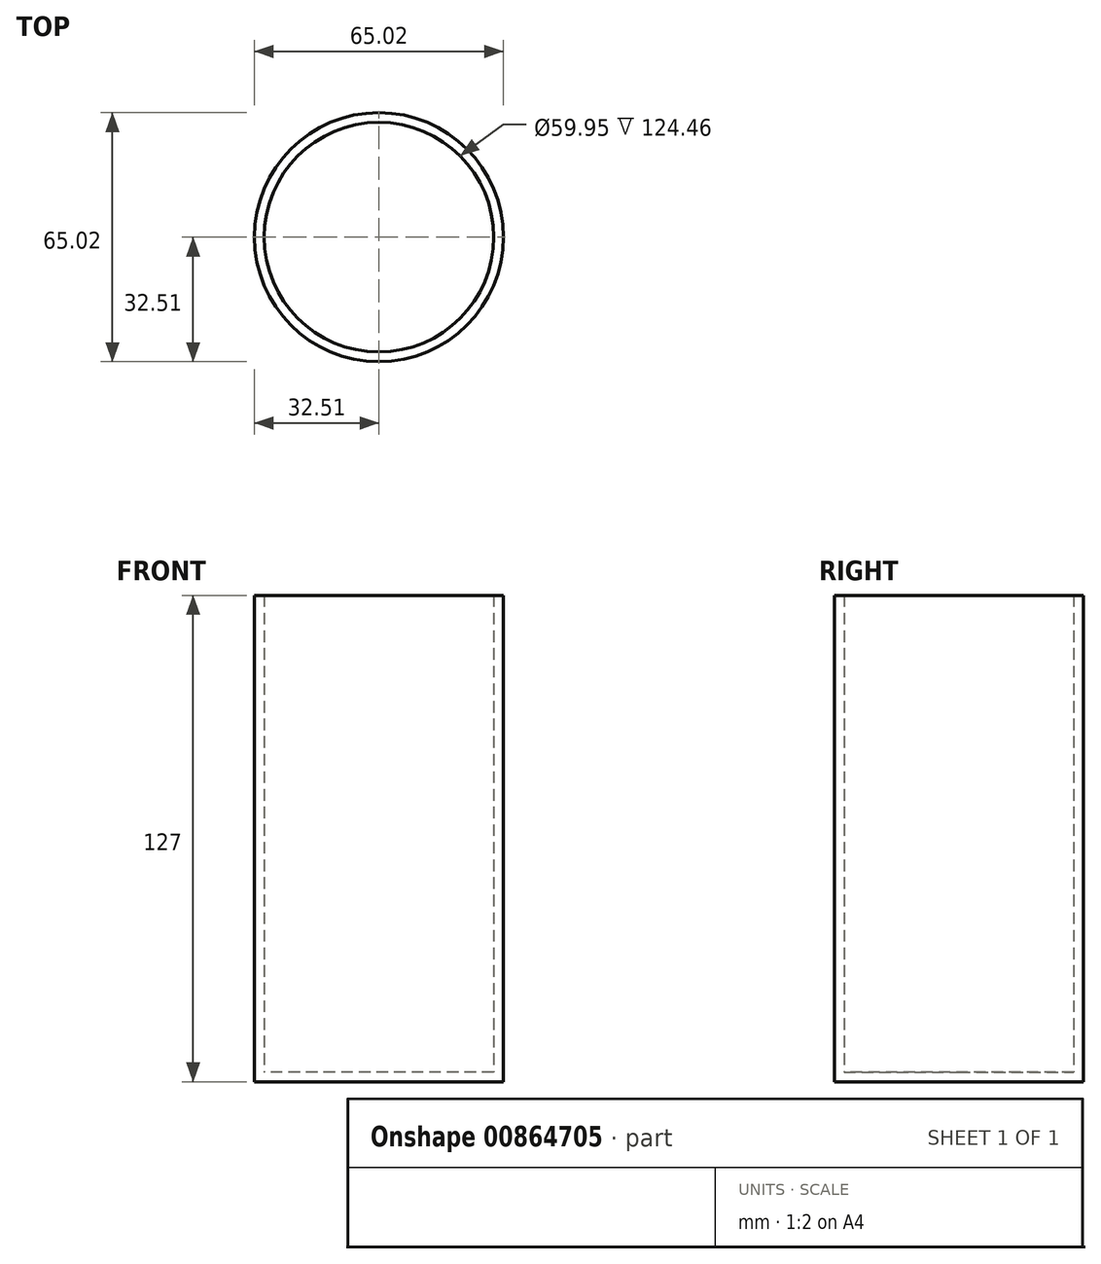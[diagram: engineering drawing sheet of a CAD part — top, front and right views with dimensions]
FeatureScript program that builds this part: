
annotation { "Feature Type Name" : "Feature", "Feature Type Description" : "" }
export const myFeature = defineFeature(function(context is Context, id is Id, definition is map)
    precondition{}
    {
        {
            var Q0;
            Q0=qCreatedBy(makeId("Top.planeOp"),FACE);
            var sketch = newSketch(context, id + "F0", { "sketchPlane" : qUnion([Q0])});
            skCircle(sketch, "E0", {"center": v(0, 0) * mm, "radius": 32.51 * mm});
            skSolve(sketch);
        }
        {
            var Q0;
            Q0=makeQuery(id+"F0.imprint","IMPRINT",FACE,{"disambiguationData":[TD([[makeQuery(id+"F0.imprint","IMPRINT",EDGE,{"derivedFrom":sQuery(id+"F0.wireOp",EDGE,"E0")}),1.0]])]});
            extrude(context, id + "F1", {"entities" : qUnion([Q0]), "endBound" : BoundingType.SYMMETRIC, "depth" : 127 * mm, "offsetDistance" : 25.4 * mm});
        }
        {
            var Q0;
            Q0=makeQuery(id+"F1.opExtrude","CAP_FACE",FACE,{"disambiguationData":[OSD([sQuery(id+"F0.wireOp",EDGE,"E0")])],"isStart":false});
            shell(context, id + "F2", {"entities" : qUnion([Q0]), "thickness" : 2.54 * mm});
        }
    });
